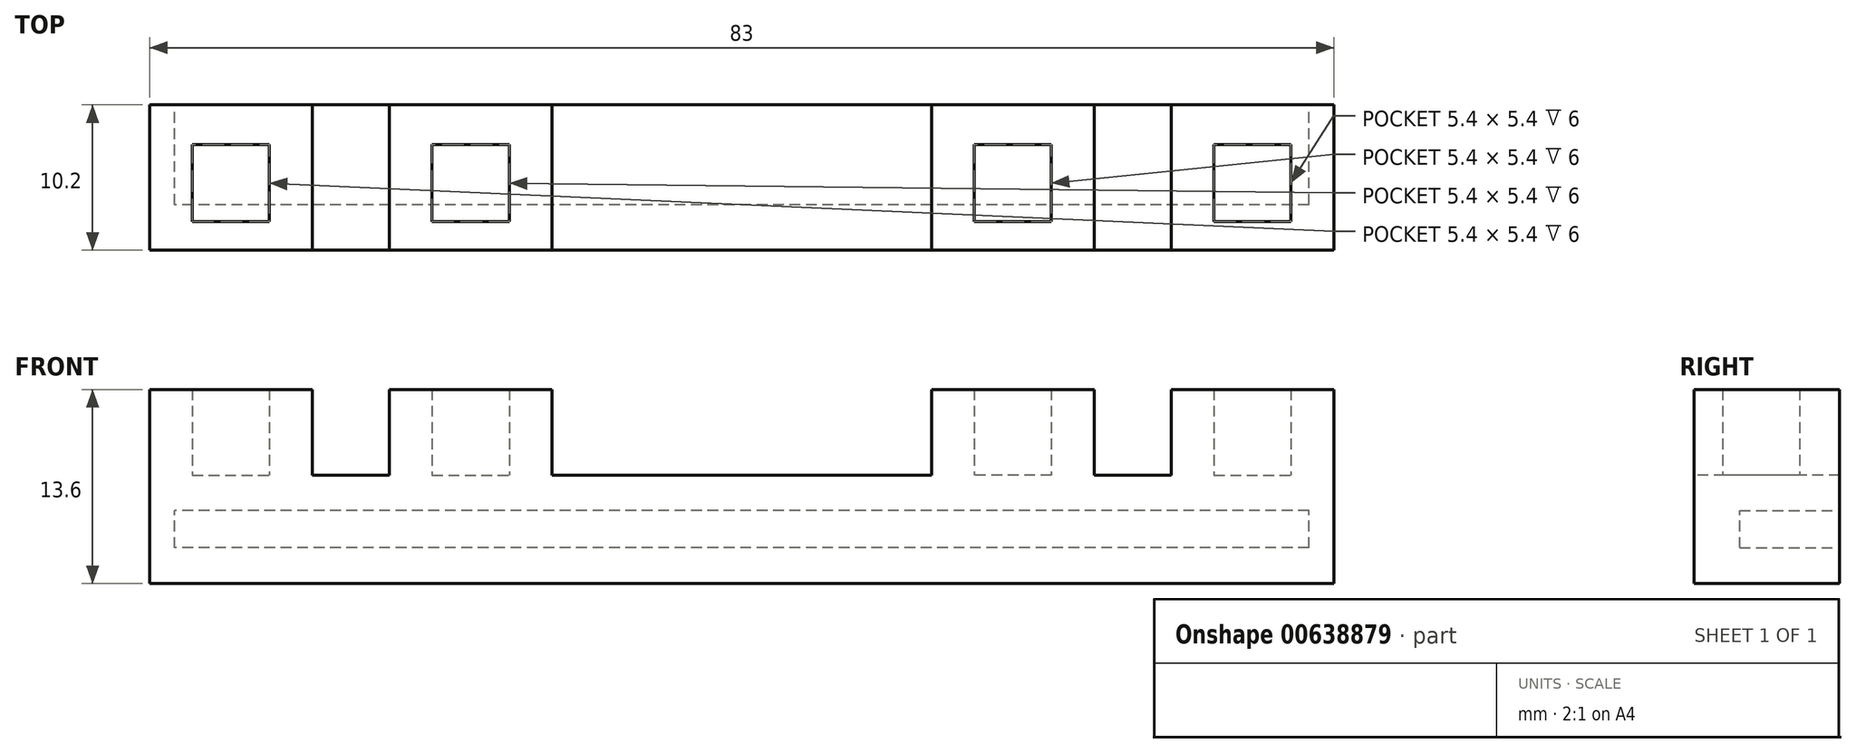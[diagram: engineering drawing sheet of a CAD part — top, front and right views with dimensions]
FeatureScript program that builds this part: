
annotation { "Feature Type Name" : "Feature", "Feature Type Description" : "" }
export const myFeature = defineFeature(function(context is Context, id is Id, definition is map)
    precondition{}
    {
        {
            var Q0;
            Q0=qCreatedBy(makeId("Front.planeOp"),FACE);
            var sketch = newSketch(context, id + "F0", { "sketchPlane" : qUnion([Q0])});
            skLineSegment(sketch, "E0.bottom", {"start": v(41.5, -3.8) * mm, "end": v(-41.5, -3.8) * mm});
            skLineSegment(sketch, "E0.top", {"start": v(41.5, 3.8) * mm, "end": v(-41.5, 3.8) * mm});
            skLineSegment(sketch, "E0.left", {"start": v(41.5, -3.8) * mm, "end": v(41.5, 3.8) * mm});
            skLineSegment(sketch, "E0.right", {"start": v(-41.5, -3.8) * mm, "end": v(-41.5, 3.8) * mm});
            skPoint(sketch, "E0.middle", {"position": v(0, 0) * mm});
            skLineSegment(sketch, "E1.bottom", {"start": v(39.75, -1.3) * mm, "end": v(-39.75, -1.3) * mm});
            skLineSegment(sketch, "E1.top", {"start": v(39.75, 1.3) * mm, "end": v(-39.75, 1.3) * mm});
            skLineSegment(sketch, "E1.left", {"start": v(39.75, -1.3) * mm, "end": v(39.75, 1.3) * mm});
            skLineSegment(sketch, "E1.right", {"start": v(-39.75, -1.3) * mm, "end": v(-39.75, 1.3) * mm});
            skSolve(sketch);
        }
        {
            var Q0;
            Q0=makeQuery(id+"F0.imprint","IMPRINT",FACE,{"disambiguationData":[TD([[makeQuery(id+"F0.imprint","IMPRINT",EDGE,{"derivedFrom":sQuery(id+"F0.wireOp",EDGE,"E0.bottom")}),-1.0]])]});
            extrude(context, id + "F1", {"entities" : qUnion([Q0]), "depth" : 7 * mm, "offsetDistance" : 25 * mm});
        }
        {
            var Q0;
            Q0=makeQuery(id+"F1.opExtrude","CAP_FACE",FACE,{"disambiguationData":[OSD([sQuery(id+"F0.wireOp",EDGE,"E0.bottom"),sQuery(id+"F0.wireOp",EDGE,"E0.top"),sQuery(id+"F0.wireOp",EDGE,"E0.left"),sQuery(id+"F0.wireOp",EDGE,"E0.right"),sQuery(id+"F0.wireOp",EDGE,"E1.bottom"),sQuery(id+"F0.wireOp",EDGE,"E1.top"),sQuery(id+"F0.wireOp",EDGE,"E1.left"),sQuery(id+"F0.wireOp",EDGE,"E1.right")])],"isStart":false});
            var sketch = newSketch(context, id + "F2", { "sketchPlane" : qUnion([Q0])});
            skLineSegment(sketch, "E2.bottom", {"start": v(-41.5, 3.8) * mm, "end": v(41.5, 3.8) * mm});
            skLineSegment(sketch, "E2.top", {"start": v(-41.5, -3.8) * mm, "end": v(41.5, -3.8) * mm});
            skLineSegment(sketch, "E2.left", {"start": v(-41.5, 3.8) * mm, "end": v(-41.5, -3.8) * mm});
            skLineSegment(sketch, "E2.right", {"start": v(41.5, 3.8) * mm, "end": v(41.5, -3.8) * mm});
            skSolve(sketch);
        }
        {
            var Q0;
            Q0=makeQuery(id+"F2.imprint","IMPRINT",FACE,{"disambiguationData":[TD([[makeQuery(id+"F2.imprint","IMPRINT",EDGE,{"derivedFrom":sQuery(id+"F2.wireOp",EDGE,"E2.bottom")}),1.0]])]});
            var Q1;
            Q1=makeQuery(id+"F2.imprint","IMPRINT",FACE,{"disambiguationData":[TD([[makeQuery(id+"F2.imprint","IMPRINT",EDGE,{"derivedFrom":makeQuery(id+"F1.opExtrude","CAP_EDGE",EDGE,{"disambiguationData":[OSD([sQuery(id+"F0.wireOp",EDGE,"E1.bottom")])],"isStart":false})}),-1.0]])]});
            extrude(context, id + "F3", {"entities" : qUnion([Q0, Q1]), "operationType" : NewBodyOperationType.ADD, "depth" : 3.2 * mm, "offsetDistance" : 25 * mm});
        }
        {
            var Q0;
            Q0=makeQuery(id+"F3.boolean.opBoolean","MERGE",FACE,{"derivedFrom":[makeQuery(id+"F1.opExtrude","SWEPT_FACE",FACE,{"disambiguationData":[OSD([sQuery(id+"F0.wireOp",EDGE,"E0.top")])]}),makeQuery(id+"F3.opExtrude","SWEPT_FACE",FACE,{"disambiguationData":[OSD([sQuery(id+"F2.wireOp",EDGE,"E2.bottom")])]})]});
            var sketch = newSketch(context, id + "F4", { "sketchPlane" : qUnion([Q0])});
            skLineSegment(sketch, "E3.bottom", {"start": v(-41.5, -10.2) * mm, "end": v(41.5, -10.2) * mm});
            skLineSegment(sketch, "E3.top", {"start": v(-41.5, 0) * mm, "end": v(41.5, 0) * mm});
            skLineSegment(sketch, "E3.left", {"start": v(-41.5, -10.2) * mm, "end": v(-41.5, 0) * mm});
            skLineSegment(sketch, "E4", {"start": v(0.5, 0) * mm, "end": v(0.5, -10.2) * mm});
            skLineSegment(sketch, "E5", {"start": v(-4.9, 0) * mm, "end": v(-4.9, -10.2) * mm});
            skLineSegment(sketch, "E6", {"start": v(-7.9, 0) * mm, "end": v(-7.9, -10.2) * mm});
            skLineSegment(sketch, "E7", {"start": v(-13.3, 0) * mm, "end": v(-13.3, -10.2) * mm});
            skLineSegment(sketch, "E8", {"start": v(-16.3, 0) * mm, "end": v(-16.3, -10.2) * mm});
            skLineSegment(sketch, "E9", {"start": v(-21.7, 0) * mm, "end": v(-21.7, -10.2) * mm});
            skLineSegment(sketch, "E10", {"start": v(-24.7, 0) * mm, "end": v(-24.7, -10.2) * mm});
            skLineSegment(sketch, "E11", {"start": v(-30.1, 0) * mm, "end": v(-30.1, -10.2) * mm});
            skLineSegment(sketch, "E12", {"start": v(-33.1, 0) * mm, "end": v(-33.1, -10.2) * mm});
            skLineSegment(sketch, "E13", {"start": v(-38.5, 0) * mm, "end": v(-38.5, -10.2) * mm});
            skLineSegment(sketch, "E14", {"start": v(0, 0) * mm, "end": v(0, -13.13) * mm, "construction": true});
            skLineSegment(sketch, "E15.MirrorCS", {"start": v(-0.5, 0) * mm, "end": v(-0.5, -10.2) * mm});
            skLineSegment(sketch, "E16", {"start": v(-41.5, -2.8) * mm, "end": v(41.5, -2.8) * mm});
            skLineSegment(sketch, "E17", {"start": v(41.5, -8.2) * mm, "end": v(-41.5, -8.2) * mm});
            skLineSegment(sketch, "E18.MirrorCS", {"start": v(16.3, 0) * mm, "end": v(16.3, -10.2) * mm});
            skLineSegment(sketch, "E19.MirrorCS", {"start": v(21.7, 0) * mm, "end": v(21.7, -10.2) * mm});
            skLineSegment(sketch, "E20.MirrorCS", {"start": v(24.7, 0) * mm, "end": v(24.7, -10.2) * mm});
            skLineSegment(sketch, "E21.MirrorCS", {"start": v(30.1, 0) * mm, "end": v(30.1, -10.2) * mm});
            skLineSegment(sketch, "E22.MirrorCS", {"start": v(33.1, 0) * mm, "end": v(33.1, -10.2) * mm});
            skLineSegment(sketch, "E23.MirrorCS", {"start": v(38.5, 0) * mm, "end": v(38.5, -10.2) * mm});
            skLineSegment(sketch, "E24.MirrorCS", {"start": v(41.5, -10.2) * mm, "end": v(41.5, 0) * mm});
            skLineSegment(sketch, "E25.MirrorCS", {"start": v(4.9, 0) * mm, "end": v(4.9, -10.2) * mm});
            skLineSegment(sketch, "E26.MirrorCS", {"start": v(13.3, 0) * mm, "end": v(13.3, -10.2) * mm});
            skLineSegment(sketch, "E27.MirrorCS", {"start": v(7.9, 0) * mm, "end": v(7.9, -10.2) * mm});
            skSolve(sketch);
        }
        {
            var Q0;
            {var subQ1=sQuery(id+"F4.wireOp",EDGE,"E3.top");var subQ3=sQuery(id+"F4.wireOp",EDGE,"E13");var subQ4=makeQuery(id+"F4.imprint","INTERSECT",VERTEX,{"derivedFrom":[subQ1,subQ3]});Q0=makeQuery(id+"F4.imprint","IMPRINT",FACE,{"disambiguationData":[TD([[makeQuery(id+"F4.imprint","IMPRINT",EDGE,{"disambiguationData":[TD([[subQ4,-1.0]])],"derivedFrom":subQ3}),-1.0]])]});}
            var Q1;
            {var subQ0=sQuery(id+"F4.wireOp",EDGE,"E12");var subQ1=sQuery(id+"F4.wireOp",EDGE,"E3.top");var subQ2=makeQuery(id+"F4.imprint","INTERSECT",VERTEX,{"derivedFrom":[subQ1,subQ0]});Q1=makeQuery(id+"F4.imprint","IMPRINT",FACE,{"disambiguationData":[TD([[makeQuery(id+"F4.imprint","IMPRINT",EDGE,{"disambiguationData":[TD([[subQ2,1.0]])],"derivedFrom":subQ1}),-1.0]])]});}
            var Q2;
            {var subQ0=sQuery(id+"F4.wireOp",EDGE,"E11");var subQ1=sQuery(id+"F4.wireOp",EDGE,"E3.top");var subQ2=makeQuery(id+"F4.imprint","INTERSECT",VERTEX,{"derivedFrom":[subQ1,subQ0]});Q2=makeQuery(id+"F4.imprint","IMPRINT",FACE,{"disambiguationData":[TD([[makeQuery(id+"F4.imprint","IMPRINT",EDGE,{"disambiguationData":[TD([[subQ2,1.0]])],"derivedFrom":subQ1}),-1.0]])]});}
            var Q3;
            {var subQ0=sQuery(id+"F4.wireOp",EDGE,"E9");var subQ1=sQuery(id+"F4.wireOp",EDGE,"E3.top");var subQ2=makeQuery(id+"F4.imprint","INTERSECT",VERTEX,{"derivedFrom":[subQ1,subQ0]});Q3=makeQuery(id+"F4.imprint","IMPRINT",FACE,{"disambiguationData":[TD([[makeQuery(id+"F4.imprint","IMPRINT",EDGE,{"disambiguationData":[TD([[subQ2,1.0]])],"derivedFrom":subQ1}),-1.0]])]});}
            var Q4;
            {var subQ0=sQuery(id+"F4.wireOp",EDGE,"E8");var subQ1=sQuery(id+"F4.wireOp",EDGE,"E3.top");var subQ2=makeQuery(id+"F4.imprint","INTERSECT",VERTEX,{"derivedFrom":[subQ1,subQ0]});Q4=makeQuery(id+"F4.imprint","IMPRINT",FACE,{"disambiguationData":[TD([[makeQuery(id+"F4.imprint","IMPRINT",EDGE,{"disambiguationData":[TD([[subQ2,1.0]])],"derivedFrom":subQ1}),-1.0]])]});}
            var Q5;
            {var subQ0=sQuery(id+"F4.wireOp",EDGE,"E7");var subQ1=sQuery(id+"F4.wireOp",EDGE,"E3.top");var subQ2=makeQuery(id+"F4.imprint","INTERSECT",VERTEX,{"derivedFrom":[subQ1,subQ0]});Q5=makeQuery(id+"F4.imprint","IMPRINT",FACE,{"disambiguationData":[TD([[makeQuery(id+"F4.imprint","IMPRINT",EDGE,{"disambiguationData":[TD([[subQ2,1.0]])],"derivedFrom":subQ1}),-1.0]])]});}
            var Q6;
            {var subQ0=sQuery(id+"F4.wireOp",EDGE,"E18.MirrorCS");var subQ1=sQuery(id+"F4.wireOp",EDGE,"E3.top");var subQ2=makeQuery(id+"F4.imprint","INTERSECT",VERTEX,{"derivedFrom":[subQ1,subQ0]});Q6=makeQuery(id+"F4.imprint","IMPRINT",FACE,{"disambiguationData":[TD([[makeQuery(id+"F4.imprint","IMPRINT",EDGE,{"disambiguationData":[TD([[subQ2,1.0]])],"derivedFrom":subQ1}),-1.0]])]});}
            var Q7;
            {var subQ0=sQuery(id+"F4.wireOp",EDGE,"E18.MirrorCS");var subQ1=sQuery(id+"F4.wireOp",EDGE,"E3.top");var subQ2=makeQuery(id+"F4.imprint","INTERSECT",VERTEX,{"derivedFrom":[subQ1,subQ0]});Q7=makeQuery(id+"F4.imprint","IMPRINT",FACE,{"disambiguationData":[TD([[makeQuery(id+"F4.imprint","IMPRINT",EDGE,{"disambiguationData":[TD([[subQ2,-1.0]])],"derivedFrom":subQ1}),-1.0]])]});}
            var Q8;
            {var subQ0=sQuery(id+"F4.wireOp",EDGE,"E19.MirrorCS");var subQ1=sQuery(id+"F4.wireOp",EDGE,"E3.top");var subQ2=makeQuery(id+"F4.imprint","INTERSECT",VERTEX,{"derivedFrom":[subQ1,subQ0]});Q8=makeQuery(id+"F4.imprint","IMPRINT",FACE,{"disambiguationData":[TD([[makeQuery(id+"F4.imprint","IMPRINT",EDGE,{"disambiguationData":[TD([[subQ2,-1.0]])],"derivedFrom":subQ1}),-1.0]])]});}
            var Q9;
            {var subQ0=sQuery(id+"F4.wireOp",EDGE,"E21.MirrorCS");var subQ1=sQuery(id+"F4.wireOp",EDGE,"E3.top");var subQ2=makeQuery(id+"F4.imprint","INTERSECT",VERTEX,{"derivedFrom":[subQ1,subQ0]});Q9=makeQuery(id+"F4.imprint","IMPRINT",FACE,{"disambiguationData":[TD([[makeQuery(id+"F4.imprint","IMPRINT",EDGE,{"disambiguationData":[TD([[subQ2,-1.0]])],"derivedFrom":subQ1}),-1.0]])]});}
            var Q10;
            {var subQ0=sQuery(id+"F4.wireOp",EDGE,"E22.MirrorCS");var subQ1=sQuery(id+"F4.wireOp",EDGE,"E3.top");var subQ2=makeQuery(id+"F4.imprint","INTERSECT",VERTEX,{"derivedFrom":[subQ1,subQ0]});Q10=makeQuery(id+"F4.imprint","IMPRINT",FACE,{"disambiguationData":[TD([[makeQuery(id+"F4.imprint","IMPRINT",EDGE,{"disambiguationData":[TD([[subQ2,-1.0]])],"derivedFrom":subQ1}),-1.0]])]});}
            var Q11;
            {var subQ0=sQuery(id+"F4.wireOp",EDGE,"E24.MirrorCS");var subQ5=sQuery(id+"F4.wireOp",EDGE,"E16");var subQ6=makeQuery(id+"F4.imprint","INTERSECT",VERTEX,{"derivedFrom":[subQ5,subQ0]});Q11=makeQuery(id+"F4.imprint","IMPRINT",FACE,{"disambiguationData":[TD([[makeQuery(id+"F4.imprint","IMPRINT",EDGE,{"disambiguationData":[TD([[subQ6,1.0]])],"derivedFrom":subQ5}),1.0]])]});}
            var Q12;
            {var subQ0=sQuery(id+"F4.wireOp",EDGE,"E16");var subQ1=sQuery(id+"F4.wireOp",EDGE,"E3.left");var subQ2=makeQuery(id+"F4.imprint","INTERSECT",VERTEX,{"derivedFrom":[subQ1,subQ0]});Q12=makeQuery(id+"F4.imprint","IMPRINT",FACE,{"disambiguationData":[TD([[makeQuery(id+"F4.imprint","IMPRINT",EDGE,{"disambiguationData":[TD([[subQ2,1.0]])],"derivedFrom":subQ1}),-1.0]])]});}
            var Q13;
            {var subQ0=sQuery(id+"F4.wireOp",EDGE,"E3.left");var subQ1=sQuery(id+"F4.wireOp",EDGE,"E3.bottom");var subQ2=makeQuery(id+"F4.imprint","INTERSECT",VERTEX,{"derivedFrom":[subQ1,subQ0]});Q13=makeQuery(id+"F4.imprint","IMPRINT",FACE,{"disambiguationData":[TD([[makeQuery(id+"F4.imprint","IMPRINT",EDGE,{"disambiguationData":[TD([[subQ2,1.0]])],"derivedFrom":subQ1}),-1.0]])]});}
            var Q14;
            {var subQ0=sQuery(id+"F4.wireOp",EDGE,"E12");var subQ1=sQuery(id+"F4.wireOp",EDGE,"E3.bottom");var subQ2=makeQuery(id+"F4.imprint","INTERSECT",VERTEX,{"derivedFrom":[subQ1,subQ0]});Q14=makeQuery(id+"F4.imprint","IMPRINT",FACE,{"disambiguationData":[TD([[makeQuery(id+"F4.imprint","IMPRINT",EDGE,{"disambiguationData":[TD([[subQ2,-1.0]])],"derivedFrom":subQ1}),-1.0]])]});}
            var Q15;
            {var subQ0=sQuery(id+"F4.wireOp",EDGE,"E11");var subQ1=sQuery(id+"F4.wireOp",EDGE,"E3.bottom");var subQ2=makeQuery(id+"F4.imprint","INTERSECT",VERTEX,{"derivedFrom":[subQ1,subQ0]});Q15=makeQuery(id+"F4.imprint","IMPRINT",FACE,{"disambiguationData":[TD([[makeQuery(id+"F4.imprint","IMPRINT",EDGE,{"disambiguationData":[TD([[subQ2,-1.0]])],"derivedFrom":subQ1}),-1.0]])]});}
            var Q16;
            {var subQ0=sQuery(id+"F4.wireOp",EDGE,"E16");var subQ1=sQuery(id+"F4.wireOp",EDGE,"E11");var subQ2=makeQuery(id+"F4.imprint","INTERSECT",VERTEX,{"derivedFrom":[subQ1,subQ0]});Q16=makeQuery(id+"F4.imprint","IMPRINT",FACE,{"disambiguationData":[TD([[makeQuery(id+"F4.imprint","IMPRINT",EDGE,{"disambiguationData":[TD([[subQ2,-1.0]])],"derivedFrom":subQ1}),-1.0]])]});}
            var Q17;
            {var subQ0=sQuery(id+"F4.wireOp",EDGE,"E9");var subQ1=sQuery(id+"F4.wireOp",EDGE,"E3.bottom");var subQ2=makeQuery(id+"F4.imprint","INTERSECT",VERTEX,{"derivedFrom":[subQ1,subQ0]});Q17=makeQuery(id+"F4.imprint","IMPRINT",FACE,{"disambiguationData":[TD([[makeQuery(id+"F4.imprint","IMPRINT",EDGE,{"disambiguationData":[TD([[subQ2,-1.0]])],"derivedFrom":subQ1}),-1.0]])]});}
            var Q18;
            {var subQ0=sQuery(id+"F4.wireOp",EDGE,"E8");var subQ1=sQuery(id+"F4.wireOp",EDGE,"E3.bottom");var subQ2=makeQuery(id+"F4.imprint","INTERSECT",VERTEX,{"derivedFrom":[subQ1,subQ0]});Q18=makeQuery(id+"F4.imprint","IMPRINT",FACE,{"disambiguationData":[TD([[makeQuery(id+"F4.imprint","IMPRINT",EDGE,{"disambiguationData":[TD([[subQ2,-1.0]])],"derivedFrom":subQ1}),-1.0]])]});}
            var Q19;
            {var subQ0=sQuery(id+"F4.wireOp",EDGE,"E16");var subQ1=sQuery(id+"F4.wireOp",EDGE,"E9");var subQ2=makeQuery(id+"F4.imprint","INTERSECT",VERTEX,{"derivedFrom":[subQ1,subQ0]});Q19=makeQuery(id+"F4.imprint","IMPRINT",FACE,{"disambiguationData":[TD([[makeQuery(id+"F4.imprint","IMPRINT",EDGE,{"disambiguationData":[TD([[subQ2,-1.0]])],"derivedFrom":subQ1}),-1.0]])]});}
            var Q20;
            {var subQ0=sQuery(id+"F4.wireOp",EDGE,"E7");var subQ1=sQuery(id+"F4.wireOp",EDGE,"E3.bottom");var subQ2=makeQuery(id+"F4.imprint","INTERSECT",VERTEX,{"derivedFrom":[subQ1,subQ0]});Q20=makeQuery(id+"F4.imprint","IMPRINT",FACE,{"disambiguationData":[TD([[makeQuery(id+"F4.imprint","IMPRINT",EDGE,{"disambiguationData":[TD([[subQ2,-1.0]])],"derivedFrom":subQ1}),-1.0]])]});}
            var Q21;
            {var subQ0=sQuery(id+"F4.wireOp",EDGE,"E24.MirrorCS");var subQ1=sQuery(id+"F4.wireOp",EDGE,"E3.bottom");var subQ2=makeQuery(id+"F4.imprint","INTERSECT",VERTEX,{"derivedFrom":[subQ1,subQ0]});Q21=makeQuery(id+"F4.imprint","IMPRINT",FACE,{"disambiguationData":[TD([[makeQuery(id+"F4.imprint","IMPRINT",EDGE,{"disambiguationData":[TD([[subQ2,-1.0]])],"derivedFrom":subQ1}),-1.0]])]});}
            var Q22;
            {var subQ0=sQuery(id+"F4.wireOp",EDGE,"E22.MirrorCS");var subQ1=sQuery(id+"F4.wireOp",EDGE,"E3.bottom");var subQ2=makeQuery(id+"F4.imprint","INTERSECT",VERTEX,{"derivedFrom":[subQ1,subQ0]});Q22=makeQuery(id+"F4.imprint","IMPRINT",FACE,{"disambiguationData":[TD([[makeQuery(id+"F4.imprint","IMPRINT",EDGE,{"disambiguationData":[TD([[subQ2,1.0]])],"derivedFrom":subQ1}),-1.0]])]});}
            var Q23;
            {var subQ0=sQuery(id+"F4.wireOp",EDGE,"E21.MirrorCS");var subQ1=sQuery(id+"F4.wireOp",EDGE,"E3.bottom");var subQ2=makeQuery(id+"F4.imprint","INTERSECT",VERTEX,{"derivedFrom":[subQ1,subQ0]});Q23=makeQuery(id+"F4.imprint","IMPRINT",FACE,{"disambiguationData":[TD([[makeQuery(id+"F4.imprint","IMPRINT",EDGE,{"disambiguationData":[TD([[subQ2,1.0]])],"derivedFrom":subQ1}),-1.0]])]});}
            var Q24;
            {var subQ0=sQuery(id+"F4.wireOp",EDGE,"E19.MirrorCS");var subQ1=sQuery(id+"F4.wireOp",EDGE,"E3.bottom");var subQ2=makeQuery(id+"F4.imprint","INTERSECT",VERTEX,{"derivedFrom":[subQ1,subQ0]});Q24=makeQuery(id+"F4.imprint","IMPRINT",FACE,{"disambiguationData":[TD([[makeQuery(id+"F4.imprint","IMPRINT",EDGE,{"disambiguationData":[TD([[subQ2,1.0]])],"derivedFrom":subQ1}),-1.0]])]});}
            var Q25;
            {var subQ0=sQuery(id+"F4.wireOp",EDGE,"E18.MirrorCS");var subQ1=sQuery(id+"F4.wireOp",EDGE,"E3.bottom");var subQ2=makeQuery(id+"F4.imprint","INTERSECT",VERTEX,{"derivedFrom":[subQ1,subQ0]});Q25=makeQuery(id+"F4.imprint","IMPRINT",FACE,{"disambiguationData":[TD([[makeQuery(id+"F4.imprint","IMPRINT",EDGE,{"disambiguationData":[TD([[subQ2,1.0]])],"derivedFrom":subQ1}),-1.0]])]});}
            var Q26;
            {var subQ0=sQuery(id+"F4.wireOp",EDGE,"E18.MirrorCS");var subQ1=sQuery(id+"F4.wireOp",EDGE,"E3.bottom");var subQ2=makeQuery(id+"F4.imprint","INTERSECT",VERTEX,{"derivedFrom":[subQ1,subQ0]});Q26=makeQuery(id+"F4.imprint","IMPRINT",FACE,{"disambiguationData":[TD([[makeQuery(id+"F4.imprint","IMPRINT",EDGE,{"disambiguationData":[TD([[subQ2,-1.0]])],"derivedFrom":subQ1}),-1.0]])]});}
            var Q27;
            {var subQ0=sQuery(id+"F4.wireOp",EDGE,"E26.MirrorCS");var subQ1=sQuery(id+"F4.wireOp",EDGE,"E16");var subQ2=makeQuery(id+"F4.imprint","INTERSECT",VERTEX,{"derivedFrom":[subQ1,subQ0]});Q27=makeQuery(id+"F4.imprint","IMPRINT",FACE,{"disambiguationData":[TD([[makeQuery(id+"F4.imprint","IMPRINT",EDGE,{"disambiguationData":[TD([[subQ2,-1.0]])],"derivedFrom":subQ1}),-1.0]])]});}
            var Q28;
            {var subQ0=sQuery(id+"F4.wireOp",EDGE,"E19.MirrorCS");var subQ1=sQuery(id+"F4.wireOp",EDGE,"E16");var subQ2=makeQuery(id+"F4.imprint","INTERSECT",VERTEX,{"derivedFrom":[subQ1,subQ0]});Q28=makeQuery(id+"F4.imprint","IMPRINT",FACE,{"disambiguationData":[TD([[makeQuery(id+"F4.imprint","IMPRINT",EDGE,{"disambiguationData":[TD([[subQ2,-1.0]])],"derivedFrom":subQ1}),-1.0]])]});}
            var Q29;
            {var subQ0=sQuery(id+"F4.wireOp",EDGE,"E21.MirrorCS");var subQ1=sQuery(id+"F4.wireOp",EDGE,"E16");var subQ2=makeQuery(id+"F4.imprint","INTERSECT",VERTEX,{"derivedFrom":[subQ1,subQ0]});Q29=makeQuery(id+"F4.imprint","IMPRINT",FACE,{"disambiguationData":[TD([[makeQuery(id+"F4.imprint","IMPRINT",EDGE,{"disambiguationData":[TD([[subQ2,-1.0]])],"derivedFrom":subQ1}),-1.0]])]});}
            var Q30;
            {var subQ0=sQuery(id+"F4.wireOp",EDGE,"E24.MirrorCS");var subQ1=sQuery(id+"F4.wireOp",EDGE,"E16");var subQ2=makeQuery(id+"F4.imprint","INTERSECT",VERTEX,{"derivedFrom":[subQ1,subQ0]});Q30=makeQuery(id+"F4.imprint","IMPRINT",FACE,{"disambiguationData":[TD([[makeQuery(id+"F4.imprint","IMPRINT",EDGE,{"disambiguationData":[TD([[subQ2,1.0]])],"derivedFrom":subQ1}),-1.0]])]});}
            var Q31;
            {var subQ0=sQuery(id+"F4.wireOp",EDGE,"E12");var subQ1=sQuery(id+"F4.wireOp",EDGE,"E3.top");var subQ2=makeQuery(id+"F4.imprint","INTERSECT",VERTEX,{"derivedFrom":[subQ1,subQ0]});Q31=makeQuery(id+"F4.imprint","IMPRINT",FACE,{"disambiguationData":[TD([[makeQuery(id+"F4.imprint","IMPRINT",EDGE,{"disambiguationData":[TD([[subQ2,-1.0]])],"derivedFrom":subQ1}),1.0]])]});}
            var Q32;
            {var subQ0=sQuery(id+"F4.wireOp",EDGE,"E11");var subQ1=sQuery(id+"F4.wireOp",EDGE,"E3.top");var subQ2=makeQuery(id+"F4.imprint","INTERSECT",VERTEX,{"derivedFrom":[subQ1,subQ0]});Q32=makeQuery(id+"F4.imprint","IMPRINT",FACE,{"disambiguationData":[TD([[makeQuery(id+"F4.imprint","IMPRINT",EDGE,{"disambiguationData":[TD([[subQ2,-1.0]])],"derivedFrom":subQ1}),1.0]])]});}
            var Q33;
            {var subQ0=sQuery(id+"F4.wireOp",EDGE,"E9");var subQ1=sQuery(id+"F4.wireOp",EDGE,"E3.top");var subQ2=makeQuery(id+"F4.imprint","INTERSECT",VERTEX,{"derivedFrom":[subQ1,subQ0]});Q33=makeQuery(id+"F4.imprint","IMPRINT",FACE,{"disambiguationData":[TD([[makeQuery(id+"F4.imprint","IMPRINT",EDGE,{"disambiguationData":[TD([[subQ2,-1.0]])],"derivedFrom":subQ1}),1.0]])]});}
            var Q34;
            {var subQ0=sQuery(id+"F4.wireOp",EDGE,"E8");var subQ1=sQuery(id+"F4.wireOp",EDGE,"E3.top");var subQ2=makeQuery(id+"F4.imprint","INTERSECT",VERTEX,{"derivedFrom":[subQ1,subQ0]});Q34=makeQuery(id+"F4.imprint","IMPRINT",FACE,{"disambiguationData":[TD([[makeQuery(id+"F4.imprint","IMPRINT",EDGE,{"disambiguationData":[TD([[subQ2,-1.0]])],"derivedFrom":subQ1}),1.0]])]});}
            var Q35;
            {var subQ0=sQuery(id+"F4.wireOp",EDGE,"E7");var subQ1=sQuery(id+"F4.wireOp",EDGE,"E3.top");var subQ2=makeQuery(id+"F4.imprint","INTERSECT",VERTEX,{"derivedFrom":[subQ1,subQ0]});Q35=makeQuery(id+"F4.imprint","IMPRINT",FACE,{"disambiguationData":[TD([[makeQuery(id+"F4.imprint","IMPRINT",EDGE,{"disambiguationData":[TD([[subQ2,-1.0]])],"derivedFrom":subQ1}),1.0]])]});}
            var Q36;
            {var subQ0=sQuery(id+"F4.wireOp",EDGE,"E18.MirrorCS");var subQ1=sQuery(id+"F4.wireOp",EDGE,"E3.top");var subQ2=makeQuery(id+"F4.imprint","INTERSECT",VERTEX,{"derivedFrom":[subQ1,subQ0]});Q36=makeQuery(id+"F4.imprint","IMPRINT",FACE,{"disambiguationData":[TD([[makeQuery(id+"F4.imprint","IMPRINT",EDGE,{"disambiguationData":[TD([[subQ2,-1.0]])],"derivedFrom":subQ1}),1.0]])]});}
            var Q37;
            {var subQ0=sQuery(id+"F4.wireOp",EDGE,"E18.MirrorCS");var subQ1=sQuery(id+"F4.wireOp",EDGE,"E3.top");var subQ2=makeQuery(id+"F4.imprint","INTERSECT",VERTEX,{"derivedFrom":[subQ1,subQ0]});Q37=makeQuery(id+"F4.imprint","IMPRINT",FACE,{"disambiguationData":[TD([[makeQuery(id+"F4.imprint","IMPRINT",EDGE,{"disambiguationData":[TD([[subQ2,1.0]])],"derivedFrom":subQ1}),1.0]])]});}
            var Q38;
            {var subQ0=sQuery(id+"F4.wireOp",EDGE,"E19.MirrorCS");var subQ1=sQuery(id+"F4.wireOp",EDGE,"E3.top");var subQ2=makeQuery(id+"F4.imprint","INTERSECT",VERTEX,{"derivedFrom":[subQ1,subQ0]});Q38=makeQuery(id+"F4.imprint","IMPRINT",FACE,{"disambiguationData":[TD([[makeQuery(id+"F4.imprint","IMPRINT",EDGE,{"disambiguationData":[TD([[subQ2,1.0]])],"derivedFrom":subQ1}),1.0]])]});}
            var Q39;
            {var subQ0=sQuery(id+"F4.wireOp",EDGE,"E22.MirrorCS");var subQ1=sQuery(id+"F4.wireOp",EDGE,"E3.top");var subQ2=makeQuery(id+"F4.imprint","INTERSECT",VERTEX,{"derivedFrom":[subQ1,subQ0]});Q39=makeQuery(id+"F4.imprint","IMPRINT",FACE,{"disambiguationData":[TD([[makeQuery(id+"F4.imprint","IMPRINT",EDGE,{"disambiguationData":[TD([[subQ2,1.0]])],"derivedFrom":subQ1}),1.0]])]});}
            var Q40;
            {var subQ0=sQuery(id+"F4.wireOp",EDGE,"E21.MirrorCS");var subQ1=sQuery(id+"F4.wireOp",EDGE,"E3.top");var subQ2=makeQuery(id+"F4.imprint","INTERSECT",VERTEX,{"derivedFrom":[subQ1,subQ0]});Q40=makeQuery(id+"F4.imprint","IMPRINT",FACE,{"disambiguationData":[TD([[makeQuery(id+"F4.imprint","IMPRINT",EDGE,{"disambiguationData":[TD([[subQ2,1.0]])],"derivedFrom":subQ1}),1.0]])]});}
            var Q41;
            {var subQ0=sQuery(id+"F4.wireOp",EDGE,"E16");var subQ1=sQuery(id+"F4.wireOp",EDGE,"E7");var subQ2=makeQuery(id+"F4.imprint","INTERSECT",VERTEX,{"derivedFrom":[subQ1,subQ0]});Q41=makeQuery(id+"F4.imprint","IMPRINT",FACE,{"disambiguationData":[TD([[makeQuery(id+"F4.imprint","IMPRINT",EDGE,{"disambiguationData":[TD([[subQ2,-1.0]])],"derivedFrom":subQ1}),-1.0]])]});}
            extrude(context, id + "F5", {"entities" : qUnion([Q0, Q1, Q2, Q3, Q4, Q5, Q6, Q7, Q8, Q9, Q10, Q11, Q12, Q13, Q14, Q15, Q16, Q17, Q18, Q19, Q20, Q21, Q22, Q23, Q24, Q25, Q26, Q27, Q28, Q29, Q30, Q31, Q32, Q33, Q34, Q35, Q36, Q37, Q38, Q39, Q40, Q41]), "operationType" : NewBodyOperationType.ADD, "depth" : 6 * mm, "offsetDistance" : 25 * mm});
        }
    });
